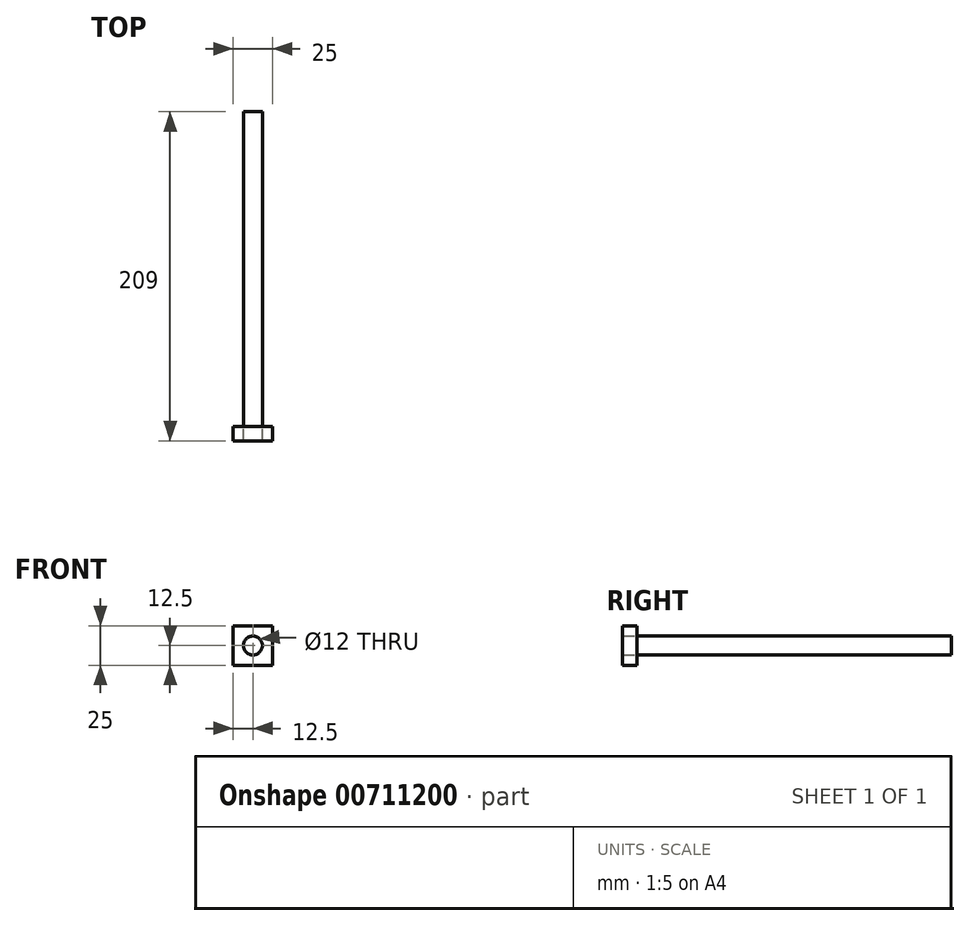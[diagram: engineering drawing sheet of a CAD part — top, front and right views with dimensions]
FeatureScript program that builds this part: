
annotation { "Feature Type Name" : "Feature", "Feature Type Description" : "" }
export const myFeature = defineFeature(function(context is Context, id is Id, definition is map)
    precondition{}
    {
        {
            var Q0;
            Q0=qCreatedBy(makeId("Front.planeOp"),FACE);
            var sketch = newSketch(context, id + "F0", { "sketchPlane" : qUnion([Q0])});
            skLineSegment(sketch, "E0.bottom", {"start": v(-12.5, 12.5) * mm, "end": v(12.5, 12.5) * mm});
            skLineSegment(sketch, "E0.top", {"start": v(-12.5, -12.5) * mm, "end": v(12.5, -12.5) * mm});
            skLineSegment(sketch, "E0.left", {"start": v(-12.5, 12.5) * mm, "end": v(-12.5, -12.5) * mm});
            skLineSegment(sketch, "E0.right", {"start": v(12.5, 12.5) * mm, "end": v(12.5, -12.5) * mm});
            skPoint(sketch, "E0.middle", {"position": v(0, 0) * mm});
            skCircle(sketch, "E1", {"center": v(0, 0) * mm, "radius": 6 * mm});
            skSolve(sketch);
        }
        {
            var Q0;
            Q0=makeQuery(id+"F0.imprint","IMPRINT",FACE,{"disambiguationData":[TD([[makeQuery(id+"F0.imprint","IMPRINT",EDGE,{"derivedFrom":sQuery(id+"F0.wireOp",EDGE,"E1")}),1.0]])]});
            extrude(context, id + "F1", {"entities" : qUnion([Q0]), "depth" : -200 * mm, "offsetDistance" : 25 * mm});
        }
        {
            var Q0;
            Q0=makeQuery(id+"F0.imprint","IMPRINT",FACE,{"disambiguationData":[TD([[makeQuery(id+"F0.imprint","IMPRINT",EDGE,{"derivedFrom":sQuery(id+"F0.wireOp",EDGE,"E1")}),1.0]])]});
            var sketch = newSketch(context, id + "F2", { "sketchPlane" : qUnion([Q0])});
            skSolve(sketch);
        }
        {
            var Q0;
            Q0 = qSketchRegion(id + "F2", true);
            var Q1;
            Q1=makeQuery(id+"F2.imprint","IMPRINT",FACE,{"disambiguationData":[TD([[makeQuery(id+"F2.imprint","IMPRINT",EDGE,{"derivedFrom":makeQuery(id+"F0.imprint","IMPRINT",EDGE,{"derivedFrom":sQuery(id+"F0.wireOp",EDGE,"E1")})}),1.0]])]});
            var Q2;
            Q2=makeQuery(id+"F0.imprint","IMPRINT",FACE,{"disambiguationData":[TD([[makeQuery(id+"F0.imprint","IMPRINT",EDGE,{"derivedFrom":sQuery(id+"F0.wireOp",EDGE,"E0.bottom")}),-1.0]])]});
            extrude(context, id + "F3", {"entities" : qUnion([Q0, Q1, Q2]), "operationType" : NewBodyOperationType.ADD, "depth" : 9 * mm, "offsetDistance" : 25 * mm});
        }
    });
